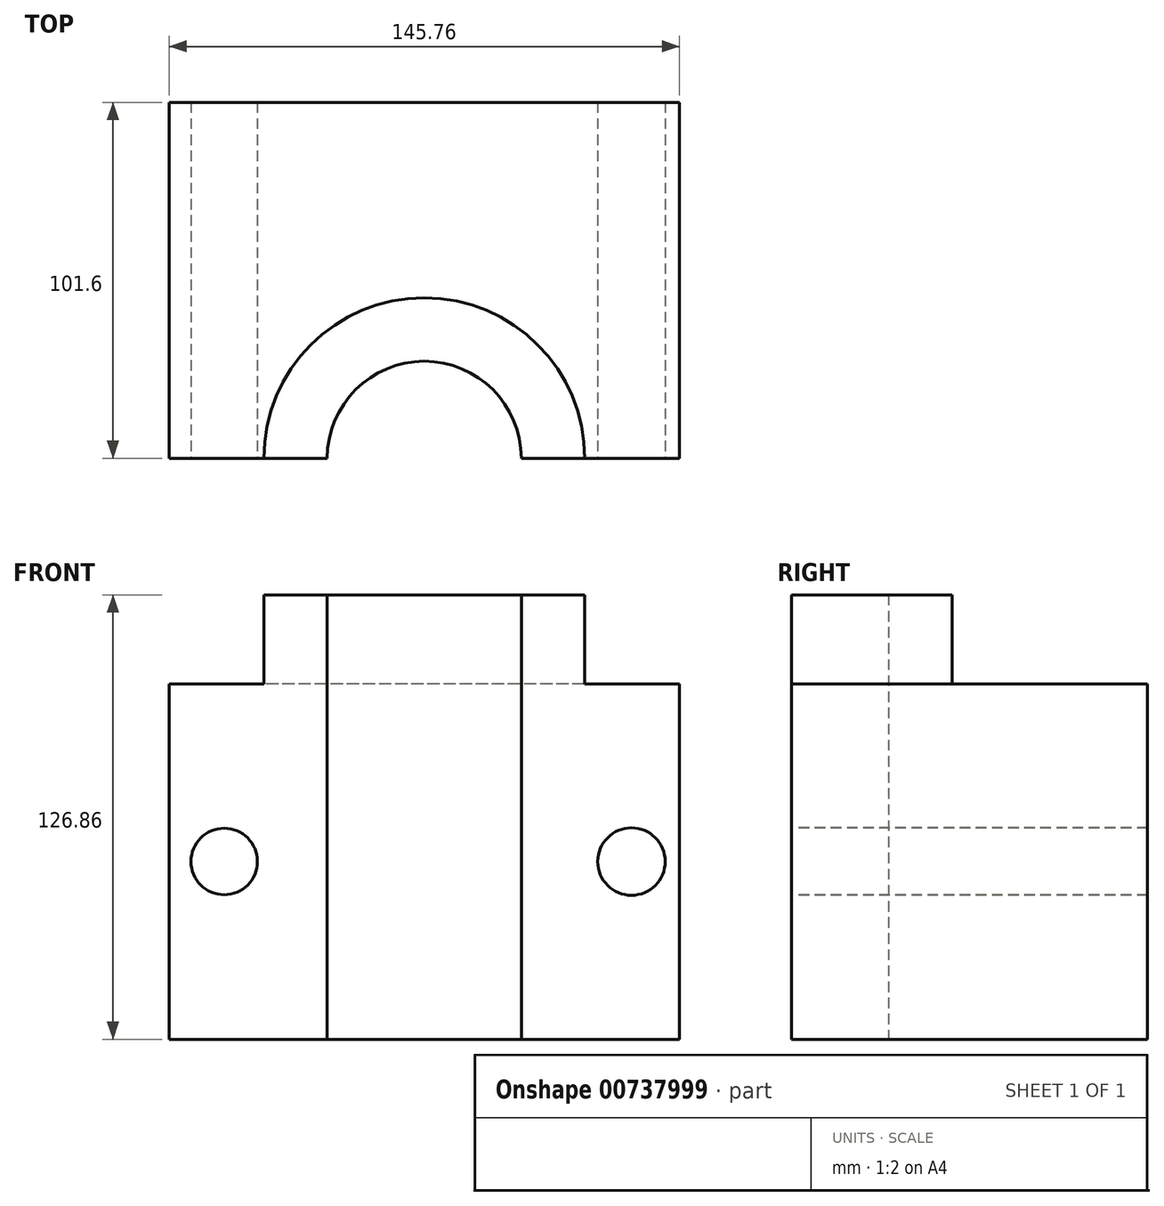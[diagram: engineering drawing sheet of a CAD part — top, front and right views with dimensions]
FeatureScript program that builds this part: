
annotation { "Feature Type Name" : "Feature", "Feature Type Description" : "" }
export const myFeature = defineFeature(function(context is Context, id is Id, definition is map)
    precondition{}
    {
        {
            var Q0;
            Q0=qCreatedBy(makeId("Front.planeOp"),FACE);
            var sketch = newSketch(context, id + "F0", { "sketchPlane" : qUnion([Q0])});
            skLineSegment(sketch, "E0.bottom", {"start": v(72.88, 50.73) * mm, "end": v(-72.88, 50.73) * mm});
            skLineSegment(sketch, "E0.top", {"start": v(72.88, -50.73) * mm, "end": v(-72.88, -50.73) * mm});
            skLineSegment(sketch, "E0.left", {"start": v(72.88, 50.73) * mm, "end": v(72.88, -50.73) * mm});
            skLineSegment(sketch, "E0.right", {"start": v(-72.88, 50.73) * mm, "end": v(-72.88, -50.73) * mm});
            skPoint(sketch, "E0.middle", {"position": v(0, 0) * mm});
            skSolve(sketch);
        }
        {
            var Q0;
            Q0 = qSketchRegion(id + "F0", true);
            extrude(context, id + "F1", {"entities" : qUnion([Q0]), "depth" : 101.6 * mm, "offsetDistance" : 25.4 * mm});
        }
        {
            var Q0;
            Q0=makeQuery(id+"F1.opExtrude","SWEPT_FACE",FACE,{"disambiguationData":[OSD([sQuery(id+"F0.wireOp",EDGE,"E0.top")])]});
            var sketch = newSketch(context, id + "F2", { "sketchPlane" : qUnion([Q0])});
            skCircle(sketch, "E1", {"center": v(0, 101.6) * mm, "radius": 46.12 * mm});
            skSolve(sketch);
        }
        {
            var Q0;
            Q0=makeQuery(id+"F1.opExtrude","SWEPT_FACE",FACE,{"disambiguationData":[OSD([sQuery(id+"F0.wireOp",EDGE,"E0.bottom")])]});
            var sketch = newSketch(context, id + "F3", { "sketchPlane" : qUnion([Q0])});
            skCircle(sketch, "E2", {"center": v(0, -101.6) * mm, "radius": 45.8 * mm});
            skSolve(sketch);
        }
        {
            var Q0;
            {var subQ0=sQuery(id+"F3.wireOp",EDGE,"E2");var subQ1=makeQuery(id+"F1.opExtrude","CAP_EDGE",EDGE,{"disambiguationData":[OSD([sQuery(id+"F0.wireOp",EDGE,"E0.bottom")])],"isStart":false});var subQ2=makeQuery(id+"F3.imprint","INTERSECT",VERTEX,{"disambiguationData":[OD(0.0)],"derivedFrom":[subQ1,subQ0]});Q0=makeQuery(id+"F3.imprint","IMPRINT",FACE,{"disambiguationData":[TD([[makeQuery(id+"F3.imprint","IMPRINT",EDGE,{"disambiguationData":[TD([[subQ2,-1.0]])],"derivedFrom":subQ0}),1.0]])]});}
            var Q1;
            {var subQ0=sQuery(id+"F2.wireOp",EDGE,"E1");var subQ1=makeQuery(id+"F1.opExtrude","CAP_EDGE",EDGE,{"disambiguationData":[OSD([sQuery(id+"F0.wireOp",EDGE,"E0.top")])],"isStart":false});var subQ2=makeQuery(id+"F2.imprint","INTERSECT",VERTEX,{"disambiguationData":[OD(0.0)],"derivedFrom":[subQ1,subQ0]});Q1=makeQuery(id+"F2.imprint","IMPRINT",FACE,{"disambiguationData":[TD([[makeQuery(id+"F2.imprint","IMPRINT",EDGE,{"disambiguationData":[TD([[subQ2,1.0]])],"derivedFrom":subQ0}),1.0]])]});}
            extrude(context, id + "F4", {"entities" : qUnion([Q0, Q1]), "operationType" : NewBodyOperationType.ADD, "depth" : 25.4 * mm, "offsetDistance" : 25.4 * mm});
        }
        {
            var Q0;
            Q0=makeQuery(id+"F1.opExtrude","SWEPT_FACE",FACE,{"disambiguationData":[OSD([sQuery(id+"F0.wireOp",EDGE,"E0.top")])]});
            var sketch = newSketch(context, id + "F5", { "sketchPlane" : qUnion([Q0])});
            skCircle(sketch, "E3", {"center": v(0, 101.6) * mm, "radius": 27.7 * mm});
            skSolve(sketch);
        }
        {
            var Q0;
            Q0 = qSketchRegion(id + "F5", true);
            extrude(context, id + "F6", {"entities" : qUnion([Q0]), "operationType" : NewBodyOperationType.REMOVE, "oppositeDirection" : true, "depth" : 127 * mm, "offsetDistance" : 25.4 * mm});
        }
        {
            var Q0;
            {var subQ1=sQuery(id+"F0.wireOp",EDGE,"E0.top");var subQ2=sQuery(id+"F0.wireOp",EDGE,"E0.right");var subQ3=sQuery(id+"F0.wireOp",EDGE,"E0.bottom");Q0=makeQuery(id+"F6.boolean.opBoolean","SPLIT",FACE,{"disambiguationData":[TD([makeQuery(id+"F1.opExtrude","SWEPT_FACE",FACE,{"disambiguationData":[OSD([subQ2])]})])],"derivedFrom":makeQuery(id+"F4.boolean.opBoolean","MERGE",FACE,{"derivedFrom":[makeQuery(id+"F1.opExtrude","CAP_FACE",FACE,{"disambiguationData":[OSD([subQ3,subQ1,sQuery(id+"F0.wireOp",EDGE,"E0.left"),subQ2])],"isStart":false}),makeQuery(id+"F4.opExtrude","SWEPT_FACE",FACE,{"disambiguationData":[OSD([subQ3])]})]})});}
            var sketch = newSketch(context, id + "F7", { "sketchPlane" : qUnion([Q0])});
            skCircle(sketch, "E4", {"center": v(-57.12, 0) * mm, "radius": 9.49 * mm});
            skPoint(sketch, "E4.centerSnap0", {"position": v(-72.88, 0) * mm});
            skCircle(sketch, "E5", {"center": v(59.14, 0) * mm, "radius": 9.63 * mm});
            skSolve(sketch);
        }
        {
            var Q0;
            Q0 = qSketchRegion(id + "F7", true);
            extrude(context, id + "F8", {"entities" : qUnion([Q0]), "operationType" : NewBodyOperationType.REMOVE, "oppositeDirection" : true, "depth" : 152.4 * mm, "offsetDistance" : 25.4 * mm});
        }
    });
